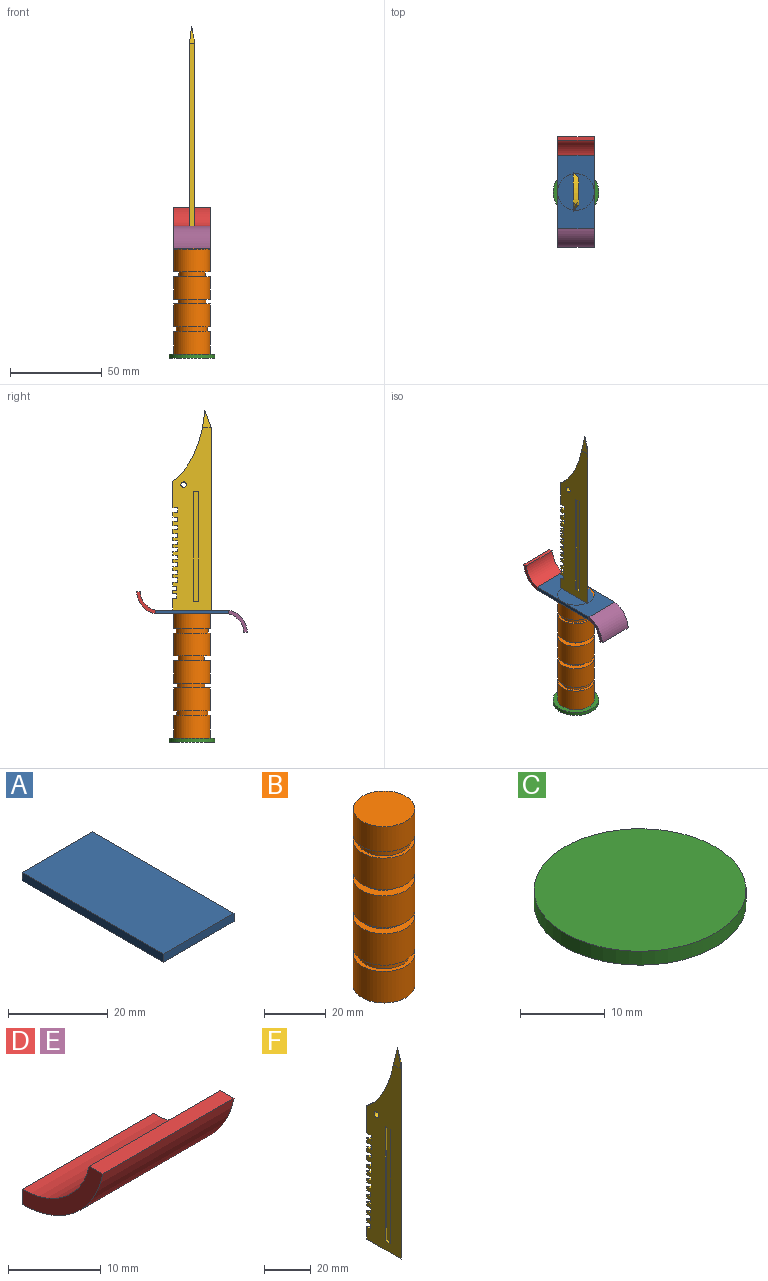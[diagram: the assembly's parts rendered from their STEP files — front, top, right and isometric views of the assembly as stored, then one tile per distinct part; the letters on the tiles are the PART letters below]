
ASSEMBLY  parts=6 mates=5
PART A: 6 faces, bbox 20x40x2 mm
  f0: plane 20x2mm, normal (0,1,0), area 40mm2, adj f1,f3,f4,f5
  f1: plane 40x2mm, normal (-1,0,0), area 80mm2, adj f0,f2,f4,f5
  f2: plane 20x2mm, normal (0,-1,0), area 40mm2, adj f1,f3,f4,f5
  f3: plane 40x2mm, normal (1,0,0), area 80mm2, adj f0,f2,f4,f5
  f4: plane 40x20mm, normal (0,0,1), area 800mm2, adj f0,f1,f2,f3
  f5: plane 40x20mm, normal (0,0,-1), area 800mm2, adj f0,f1,f2,f3
PART B: 19 faces, bbox 20x20x70 mm
  f0: cylinder r=10mm len=20mm, axis (0,0,-1), area 785.4mm2, adj f12,f14
  f1: cylinder r=10mm len=20mm, axis (0,0,-1), area 785.4mm2, adj f9,f11
  f2: cylinder r=10mm len=20mm, axis (0,0,-1), area 785.4mm2, adj f6,f8
  f3: cylinder r=10mm len=20mm, axis (0,0,-1), area 785.4mm2, adj f4,f5
  f4: plane 20x20mm, normal (0,0,-1), area 314.2mm2, adj f3
  f5: plane 20x20mm, normal (0,0,1), area 88.4mm2, adj f3,f7
  f6: plane 20x20mm, normal (0,0,-1), area 88.4mm2, adj f2,f7
  f7: cylinder r=8.48mm len=16.95mm, axis (0,0,1), area 133.2mm2, adj f5,f6
  f8: plane 20x20mm, normal (0,0,1), area 131.7mm2, adj f2,f10
  f9: plane 20x20mm, normal (0,0,-1), area 131.7mm2, adj f1,f10
  f10: cylinder r=7.62mm len=15.24mm, axis (0,0,1), area 119.7mm2, adj f8,f9
  f11: plane 20x20mm, normal (0,0,1), area 153.8mm2, adj f1,f13
  f12: plane 20x20mm, normal (0,0,-1), area 153.8mm2, adj f0,f13
  f13: cylinder r=7.15mm len=14.29mm, axis (0,0,1), area 112.2mm2, adj f11,f12
  f14: plane 20x20mm, normal (0,0,1), area 76.1mm2, adj f0,f16
  f15: plane 20x20mm, normal (0,0,-1), area 76.1mm2, adj f16,f18
  f16: cylinder r=8.7mm len=17.41mm, axis (0,0,1), area 136.7mm2, adj f14,f15
  f17: plane 20x20mm, normal (0,0,1), area 314.2mm2, adj f18
  f18: cylinder r=10mm len=20mm, axis (0,0,-1), area 628.3mm2, adj f15,f17
PART C: 3 faces, bbox 25x25x2 mm
  f0: cylinder r=12.5mm len=25mm, axis (0,0,-1), area 157.1mm2, adj f1,f2
  f1: plane 25x25mm, normal (0,0,1), area 490.9mm2, adj f0
  f2: plane 25x25mm, normal (0,0,-1), area 490.9mm2, adj f0
PART D: 6 faces, bbox 20x12.3x10.1 mm
  f0: plane 20x2mm, normal (0,1,0), area 40mm2, adj f1,f3,f4,f5
  f1: cylinder r=10.5mm len=20mm, axis (-1,0,0), area 282.3mm2, adj f0,f2,f4,f5
  f2: plane 20x2.04mm, normal (0,-0.01,1), area 40.8mm2, adj f1,f3,f4,f5
  f3: cylinder r=12.5mm len=20mm, axis (-1,0,0), area 345mm2, adj f0,f2,f4,f5
  f4: plane 12.27x10.14mm, normal (1,0,0), area 31.4mm2, adj f0,f1,f2,f3
  f5: plane 12.27x10.14mm, normal (-1,0,0), area 31.4mm2, adj f0,f1,f2,f3
PART E: same geometry as D
PART F: 57 faces, bbox 3x21x109.3 mm
  f0: plane 100x21mm, normal (-1,0,0), area 1534.7mm2, adj f2,f3,f4,f5,f6,f7,f8,f9
  f1: plane 100x15mm, normal (1,0,0), area 1087.2mm2, adj f2,f12,f40,f41,f42,f43,f44,f51
  f2: plane 21x3mm, normal (0,0,-1), area 54mm2, adj f0,f1,f51,f52
  f3: plane 2.62x2.62mm, normal (0,0,-1), area 3.4mm2, adj f0,f5,f51
  f4: plane 2.62x2.62mm, normal (0,0,1), area 3.4mm2, adj f0,f5,f51
  f5: plane 2.62x1.78mm, normal (0,1,0), area 4.6mm2, adj f0,f3,f4,f51
  f6: plane 2.49x2.49mm, normal (0,0,-1), area 3.1mm2, adj f0,f8,f51
  f7: plane 2.49x2.49mm, normal (0,0,1), area 3.1mm2, adj f0,f8,f51
  f8: plane 2.49x1.87mm, normal (0,1,0), area 4.6mm2, adj f0,f6,f7,f51
  f9: plane 2.64x2.64mm, normal (0,0,1), area 3.5mm2, adj f0,f11,f51
  f10: plane 2.64x2.64mm, normal (0,0,-1), area 3.5mm2, adj f0,f11,f51
  f11: plane 2.64x2.03mm, normal (0,1,0), area 5.3mm2, adj f0,f9,f10,f51
  f12: cylinder r=1.5mm len=3mm, axis (1,0,0), area 28.3mm2, adj f0,f1
  f13: plane 2.6x2.6mm, normal (0,0,-1), area 3.4mm2, adj f0,f15,f51
  f14: plane 2.6x2.6mm, normal (0,0,1), area 3.4mm2, adj f0,f15,f51
  f15: plane 2.6x2.16mm, normal (0,1,0), area 5.6mm2, adj f0,f13,f14,f51
  f16: plane 2.59x2.59mm, normal (0,0,1), area 3.4mm2, adj f0,f18,f51
  f17: plane 2.59x2.59mm, normal (0,0,-1), area 3.4mm2, adj f0,f18,f51
  f18: plane 2.59x2.26mm, normal (0,1,0), area 5.8mm2, adj f0,f16,f17,f51
  f19: plane 2.46x2.46mm, normal (0,0,-1), area 3mm2, adj f0,f21,f51
  f20: plane 2.46x2.46mm, normal (0,0,1), area 3mm2, adj f0,f21,f51
  f21: plane 2.6x2.46mm, normal (0,1,0), area 6.4mm2, adj f0,f19,f20,f51
  f22: plane 2.2x2.2mm, normal (0,0,-1), area 2.4mm2, adj f0,f24,f51
  f23: plane 2.2x2.2mm, normal (0,0,1), area 2.4mm2, adj f0,f24,f51
  f24: plane 2.26x2.2mm, normal (0,1,0), area 5mm2, adj f0,f22,f23,f51
  f25: plane 2.64x2.64mm, normal (0,0,1), area 3.5mm2, adj f0,f27,f51
  f26: plane 2.64x2.64mm, normal (0,0,-1), area 3.5mm2, adj f0,f27,f51
  f27: plane 2.64x2.2mm, normal (0,1,0), area 5.8mm2, adj f0,f25,f26,f51
  f28: plane 2.71x2.71mm, normal (0,0,1), area 3.7mm2, adj f0,f30,f51
  f29: plane 2.71x2.71mm, normal (0,0,-1), area 3.7mm2, adj f0,f30,f51
  f30: plane 2.71x2.05mm, normal (0,1,0), area 5.6mm2, adj f0,f28,f29,f51
  f31: plane 2.71x2.71mm, normal (0,0,1), area 3.7mm2, adj f0,f33,f51
  f32: plane 2.71x2.71mm, normal (0,0,-1), area 3.7mm2, adj f0,f33,f51
  f33: plane 2.71x2.35mm, normal (0,1,0), area 6.4mm2, adj f0,f31,f32,f51
  f34: plane 2.7x2.7mm, normal (0,0,1), area 3.6mm2, adj f0,f36,f51
  f35: plane 2.7x2.7mm, normal (0,0,-1), area 3.6mm2, adj f0,f36,f51
  f36: plane 2.7x2.41mm, normal (0,1,0), area 6.5mm2, adj f0,f34,f35,f51
  f37: plane 2.23x2.23mm, normal (0,0,1), area 2.5mm2, adj f0,f39,f51
  f38: plane 2.23x2.23mm, normal (0,0,-1), area 2.5mm2, adj f0,f39,f51
  f39: plane 2.31x2.23mm, normal (0,1,0), area 5.2mm2, adj f0,f37,f38,f51
  f40: extruded ~29.67x16.28mm, area 98.2mm2, adj f0,f1,f51,f53
  f41: plane 3x1mm, normal (0,0,-1), area 3mm2, adj f1,f42,f44,f45
  f42: plane 60x1mm, normal (0,1,0), area 60mm2, adj f1,f41,f43,f45
  f43: plane 3x1mm, normal (0,0,1), area 3mm2, adj f1,f42,f44,f45
  f44: plane 60x1mm, normal (0,-1,0), area 60mm2, adj f1,f41,f43,f45
  f45: plane 60x3mm, normal (1,0,0), area 180mm2, adj f41,f42,f43,f44
  f46: plane 3x1mm, normal (0,0,-1), area 3mm2, adj f0,f47,f49,f50
  f47: plane 60x1mm, normal (0,-1,0), area 60mm2, adj f0,f46,f48,f50
  f48: plane 3x1mm, normal (0,0,1), area 3mm2, adj f0,f47,f49,f50
  f49: plane 60x1mm, normal (0,1,0), area 60mm2, adj f0,f46,f48,f50
  f50: plane 60x3mm, normal (-1,0,0), area 180mm2, adj f46,f47,f48,f49
  f51: plane 72.73x3mm, normal (0.71,0.71,0), area 208.6mm2, adj f0,f1,f2,f3,f4,f5,f6,f7
  f52: plane 100x3mm, normal (0.71,-0.71,0), area 424.3mm2, adj f0,f1,f2,f55
  f53: plane 9.3x3mm, normal (0,0.99,0.13), area 14.1mm2, adj f40,f54,f56
  f54: plane 9.3x4.72mm, normal (-0.99,0,0.13), area 22.1mm2, adj f0,f53,f55
  f55: plane 9.3x3.51mm, normal (0.7,-0.7,0.17), area 20mm2, adj f52,f54,f56
  f56: plane 9.3x1.77mm, normal (0.98,0,0.19), area 8.1mm2, adj f1,f53,f55
PLACE A t=(51.72,-2.66,44.96)mm
PLACE B t=(14.17,-2.6,-23.04)mm
PLACE C rot(axis=(1,0,0),180deg) t=(14.17,88.78,-23.04)mm
PLACE D rot(axis=(1,0,0),89.6deg) t=(31.57,44.01,71.22)mm
PLACE E rot(axis=(-1,0,0),90.4deg) t=(31.57,8.36,20.7)mm
PLACE F t=(-4.65,27.83,46.96)mm
MATE fastened E.f2 <-> A.f2  axis (0,1,0) through (14.17,6.18,45.96)mm
MATE fastened F.f2 <-> B.f0  axis (0,0,-1) through (14.17,26.18,46.96)mm
MATE fastened A.f4 <-> B.f0  axis (0,0,1) through (14.17,26.18,46.96)mm
MATE fastened D.f2 <-> A.f0  axis (0,-1,0) through (14.17,46.18,45.96)mm
MATE fastened B.f0 <-> C.f0  axis (0,0,-1) through (14.17,26.18,-23.04)mm
